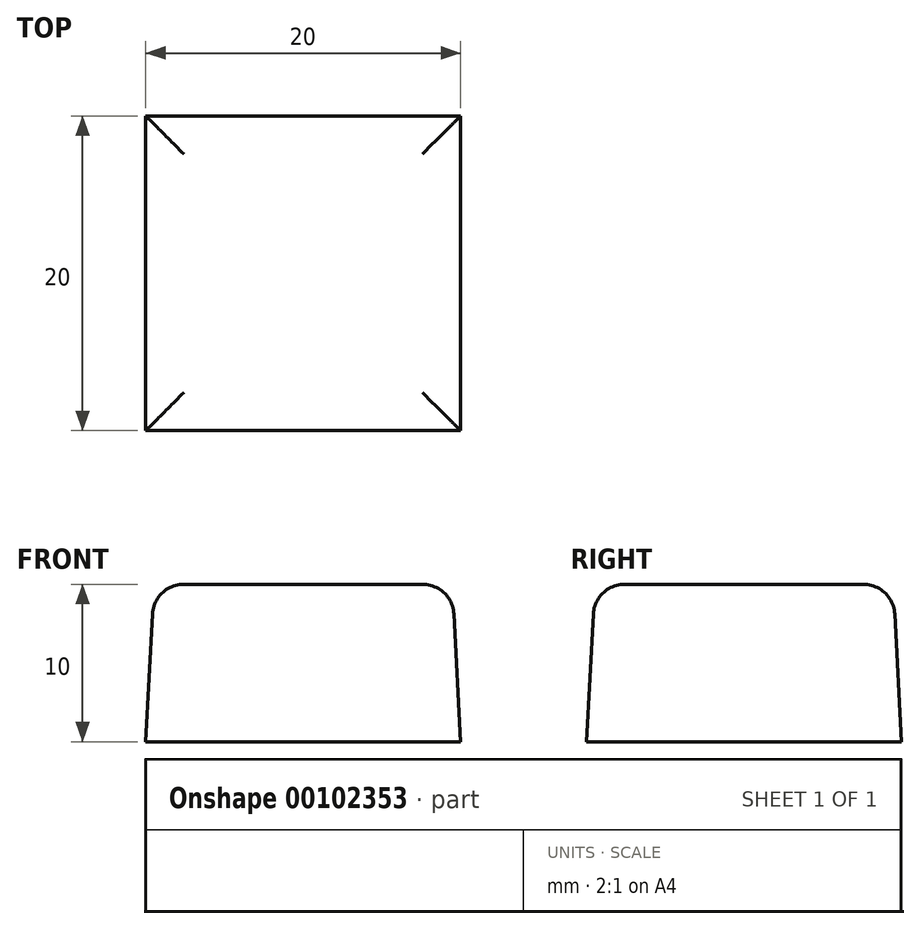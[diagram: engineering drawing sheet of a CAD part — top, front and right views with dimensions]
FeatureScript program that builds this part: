
annotation { "Feature Type Name" : "Feature", "Feature Type Description" : "" }
export const myFeature = defineFeature(function(context is Context, id is Id, definition is map)
    precondition{}
    {
        {
            var Q0;
            Q0=qCreatedBy(makeId("Top.planeOp"),FACE);
            var sketch = newSketch(context, id + "F0", { "sketchPlane" : qUnion([Q0])});
            skLineSegment(sketch, "E0.bottom", {"start": v(0, 0) * mm, "end": v(0, 0) * mm});
            skLineSegment(sketch, "E0.top", {"start": v(0, 4.5) * mm, "end": v(0, 4.5) * mm});
            skLineSegment(sketch, "E0.left", {"start": v(0, 0) * mm, "end": v(0, 4.5) * mm});
            skLineSegment(sketch, "E0.right", {"start": v(0, 0) * mm, "end": v(0, 4.5) * mm});
            skLineSegment(sketch, "E1.left", {"start": v(0, 4.5) * mm, "end": v(0, 0) * mm});
            skLineSegment(sketch, "E1.right", {"start": v(0, 4.5) * mm, "end": v(0, 0) * mm});
            skLineSegment(sketch, "E2.bottom", {"start": v(-10, 10) * mm, "end": v(10, 10) * mm});
            skLineSegment(sketch, "E2.top", {"start": v(-10, -10) * mm, "end": v(10, -10) * mm});
            skLineSegment(sketch, "E2.left", {"start": v(-10, 10) * mm, "end": v(-10, -10) * mm});
            skLineSegment(sketch, "E2.right", {"start": v(10, 10) * mm, "end": v(10, -10) * mm});
            skPoint(sketch, "E2.middle", {"position": v(0, 0) * mm});
            skSolve(sketch);
        }
        {
            var Q0;
            Q0=makeQuery(id+"F0.imprint","IMPRINT",FACE,{"disambiguationData":[TD([[makeQuery(id+"F0.imprint","IMPRINT",EDGE,{"derivedFrom":sQuery(id+"F0.wireOp",EDGE,"E2.bottom")}),-1.0]])]});
            extrude(context, id + "F1", {"entities" : qUnion([Q0]), "depth" : 10 * mm, "hasDraft" : true, "draftAngle" : 3 * degree, "draftPullDirection" : true});
        }
        {
            var Q0;
            Q0=makeQuery(id+"F1.opExtrude","CAP_EDGE",EDGE,{"disambiguationData":[OSD([sQuery(id+"F0.wireOp",EDGE,"E2.bottom")])],"isStart":false});
            var Q1;
            Q1=makeQuery(id+"F1.opExtrude","CAP_EDGE",EDGE,{"disambiguationData":[OSD([sQuery(id+"F0.wireOp",EDGE,"E2.left")])],"isStart":false});
            var Q2;
            Q2=makeQuery(id+"F1.opExtrude","CAP_EDGE",EDGE,{"disambiguationData":[OSD([sQuery(id+"F0.wireOp",EDGE,"E2.right")])],"isStart":false});
            var Q3;
            Q3=makeQuery(id+"F1.opExtrude","CAP_EDGE",EDGE,{"disambiguationData":[OSD([sQuery(id+"F0.wireOp",EDGE,"E2.top")])],"isStart":false});
            fillet(context, id + "F2", {"entities" : qUnion([Q0, Q1, Q2, Q3]), "radius" : 2 * mm, "tangentPropagation" : true, "allowEdgeOverflow" : false});
        }
    });
